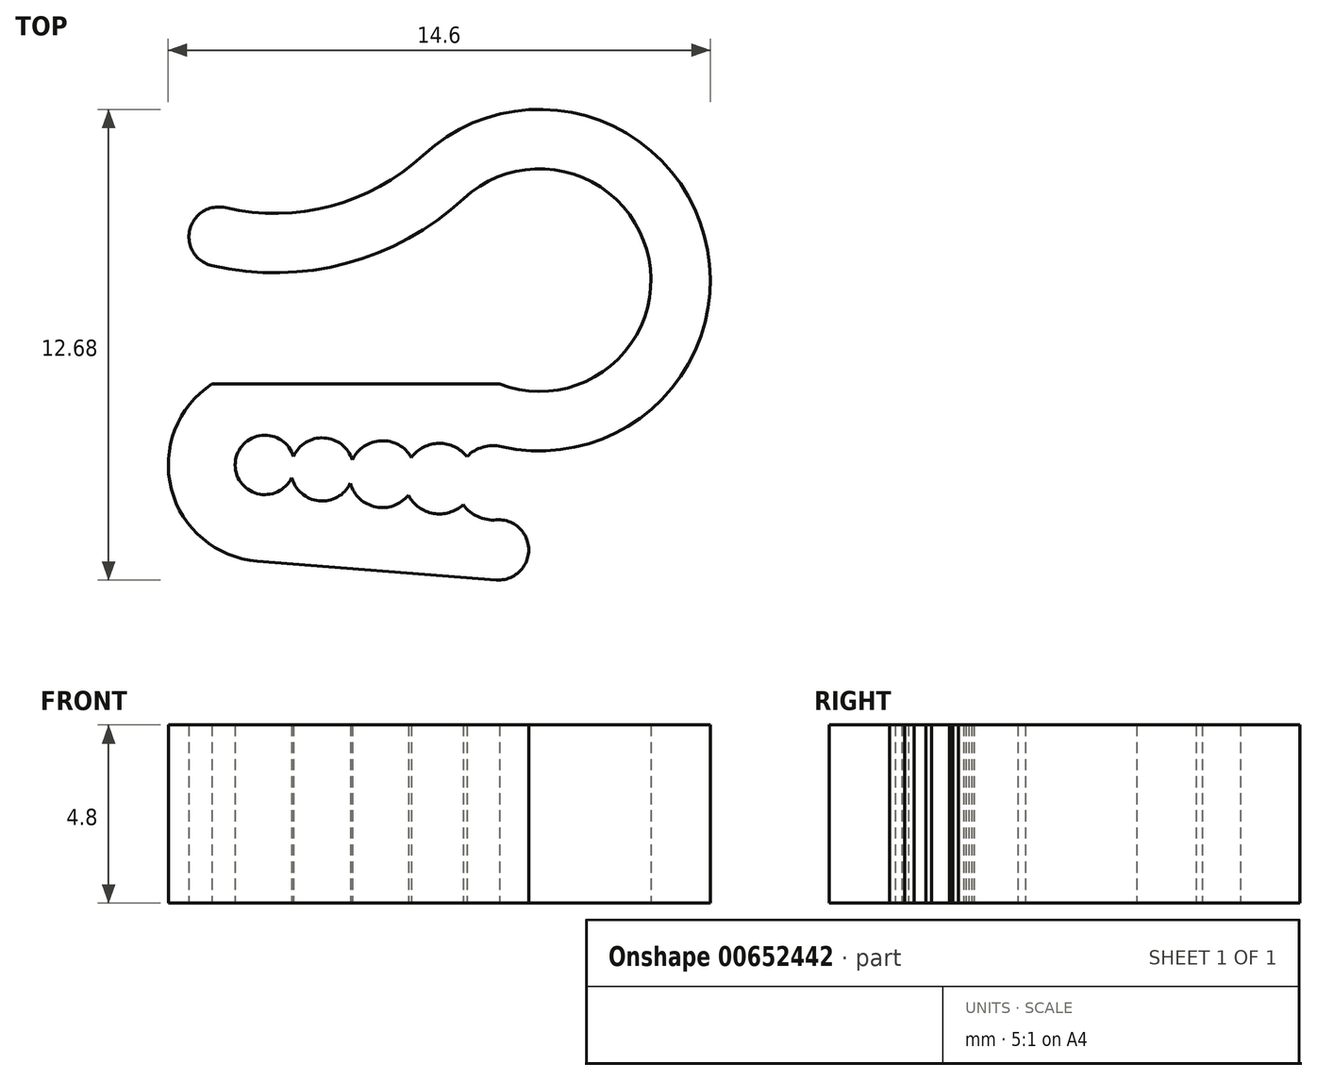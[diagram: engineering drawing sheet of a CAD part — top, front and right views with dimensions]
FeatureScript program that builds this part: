
annotation { "Feature Type Name" : "Feature", "Feature Type Description" : "" }
export const myFeature = defineFeature(function(context is Context, id is Id, definition is map)
    precondition{}
    {
        {
            var Q0;
            Q0=qCreatedBy(makeId("Top.planeOp"),FACE);
            var sketch = newSketch(context, id + "F0", { "sketchPlane" : qUnion([Q0])});
            skArc(sketch, "E0", {"start": v(-1.08, -2.8) * mm, "mid": v(2.95, 0.57) * mm, "end": v(-2.04, 2.2) * mm});
            skLineSegment(sketch, "E1", {"start": v(-1.08, -2.8) * mm, "end": v(-8.82, -2.8) * mm});
            skArc(sketch, "E2", {"start": v(-8.82, 0.4) * mm, "mid": v(-5.2, 0.45) * mm, "end": v(-2.04, 2.2) * mm});
            skArc(sketch, "E3.0", {"start": v(-8.46, 1.95) * mm, "mid": v(-5.62, 2) * mm, "end": v(-3.13, 3.37) * mm});
            skArc(sketch, "E3.1", {"start": v(-1.03, -4.48) * mm, "mid": v(4.44, 1.2) * mm, "end": v(-3.13, 3.37) * mm});
            skArc(sketch, "E4", {"start": v(-8.82, 0.4) * mm, "mid": v(-9.42, 1.35) * mm, "end": v(-8.46, 1.95) * mm});
            skArc(sketch, "E5", {"start": v(-1.03, -4.48) * mm, "mid": v(-1.52, -4.5) * mm, "end": v(-1.95, -4.75) * mm});
            skArc(sketch, "E6", {"start": v(-3.45, -4.77) * mm, "mid": v(-4.27, -4.33) * mm, "end": v(-5.04, -4.84) * mm});
            skArc(sketch, "E7", {"start": v(-5.04, -4.84) * mm, "mid": v(-5.8, -4.25) * mm, "end": v(-6.63, -4.75) * mm});
            skArc(sketch, "E8", {"start": v(-6.63, -4.75) * mm, "mid": v(-8.2, -4.91) * mm, "end": v(-6.67, -5.32) * mm});
            skArc(sketch, "E9", {"start": v(-1.95, -4.75) * mm, "mid": v(-2.7, -4.4) * mm, "end": v(-3.45, -4.77) * mm});
            skArc(sketch, "E10", {"start": v(-8.82, -2.8) * mm, "mid": v(-9.91, -5.62) * mm, "end": v(-7.6, -7.57) * mm});
            skLineSegment(sketch, "E11", {"start": v(-7.6, -7.57) * mm, "end": v(-1.17, -8.07) * mm});
            skArc(sketch, "E12", {"start": v(-1.17, -8.07) * mm, "mid": v(-0.3, -7.26) * mm, "end": v(-1.17, -6.46) * mm});
            skPoint(sketch, "E12.first.point", {"position": v(-1.17, -6.46) * mm});
            skPoint(sketch, "E12.second.point", {"position": v(-1.17, -8.07) * mm});
            skPoint(sketch, "E12.third.point", {"position": v(-0.46, -6.77) * mm});
            skArc(sketch, "E13.trimOffspring", {"start": v(-2.06, -6.05) * mm, "mid": v(-1.66, -6.37) * mm, "end": v(-1.17, -6.46) * mm});
            skArc(sketch, "E14.trimOffspring", {"start": v(-3.53, -5.8) * mm, "mid": v(-2.85, -6.28) * mm, "end": v(-2.06, -6.05) * mm});
            skArc(sketch, "E15.trimOffspring", {"start": v(-5.1, -5.48) * mm, "mid": v(-4.4, -6.1) * mm, "end": v(-3.53, -5.8) * mm});
            skArc(sketch, "E16.trimOffspring", {"start": v(-6.67, -5.32) * mm, "mid": v(-5.94, -5.94) * mm, "end": v(-5.1, -5.48) * mm});
            skLineSegment(sketch, "E17", {"start": v(-7.4, -4.98) * mm, "end": v(-1.25, -5.46) * mm, "construction": true});
            skSolve(sketch);
        }
        {
            var Q0;
            Q0 = qSketchRegion(id + "F0", true);
            extrude(context, id + "F1", {"entities" : qUnion([Q0]), "depth" : 4.8 * mm, "offsetDistance" : 25 * mm});
        }
    });
